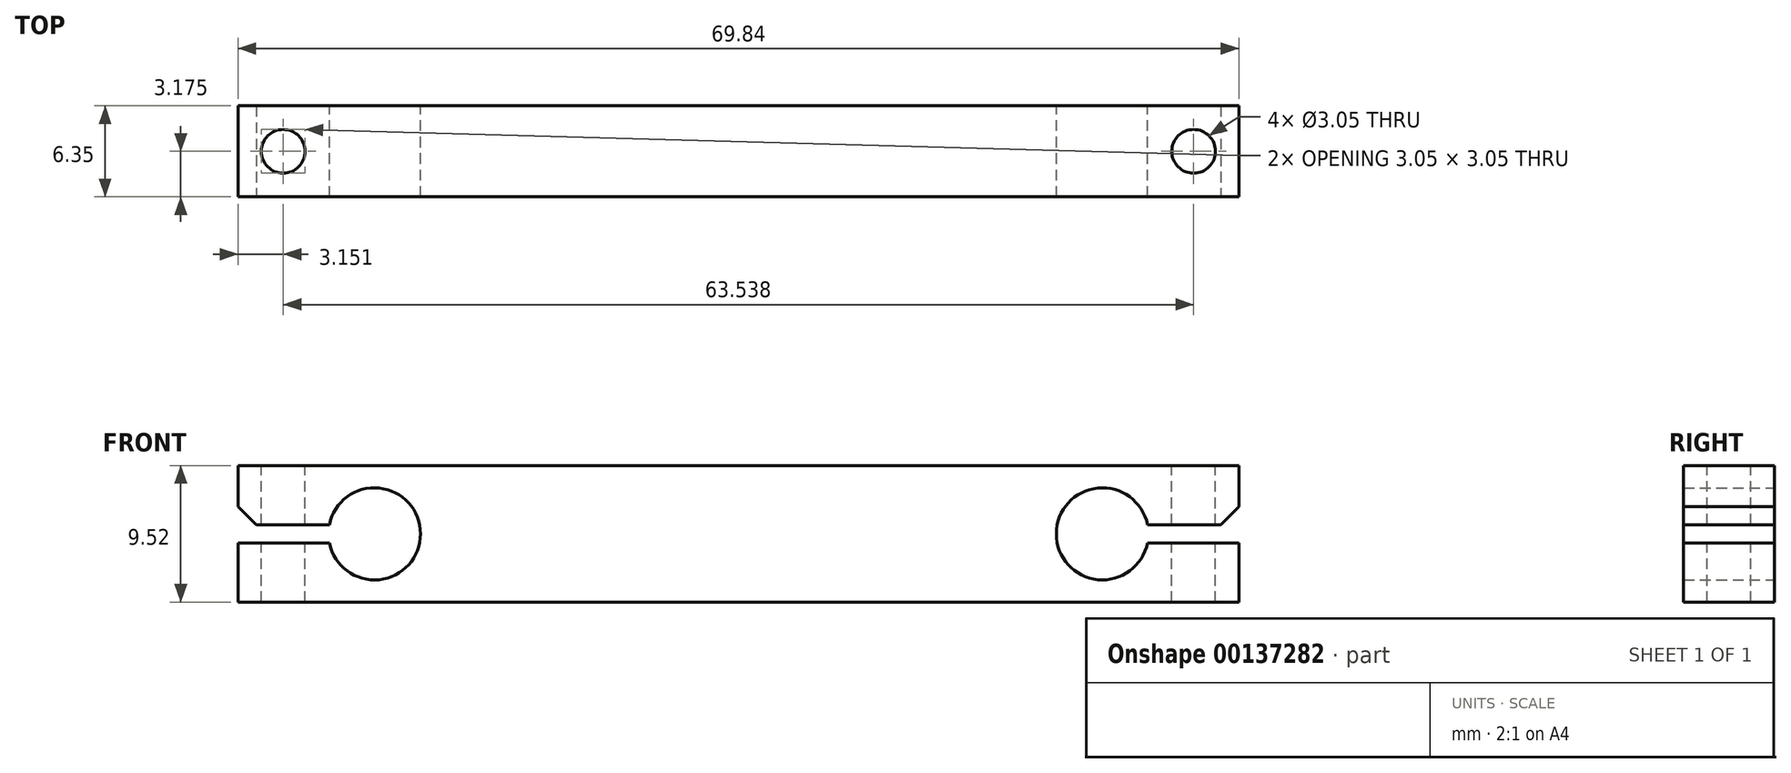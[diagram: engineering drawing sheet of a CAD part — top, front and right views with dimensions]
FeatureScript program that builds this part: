
annotation { "Feature Type Name" : "Feature", "Feature Type Description" : "" }
export const myFeature = defineFeature(function(context is Context, id is Id, definition is map)
    precondition{}
    {
        {
            var Q0;
            Q0=qCreatedBy(makeId("Front.planeOp"),FACE);
            var sketch = newSketch(context, id + "F0", { "sketchPlane" : qUnion([Q0])});
            skCircle(sketch, "E0", {"center": v(25.4, 0) * mm, "radius": 3.21 * mm});
            skLineSegment(sketch, "E1.bottom", {"start": v(0, 4.76) * mm, "end": v(34.93, 4.76) * mm});
            skLineSegment(sketch, "E1.top", {"start": v(0, -4.76) * mm, "end": v(34.93, -4.76) * mm});
            skLineSegment(sketch, "E1.left", {"start": v(0, 4.76) * mm, "end": v(0, -4.76) * mm});
            skLineSegment(sketch, "E1.right", {"start": v(34.93, 4.76) * mm, "end": v(34.93, -4.76) * mm});
            skPoint(sketch, "E1.middle", {"position": v(17.46, 0) * mm});
            skSolve(sketch);
        }
        {
            var Q0;
            Q0 = qSketchRegion(id + "F0", true);
            extrude(context, id + "F1", {"entities" : qUnion([Q0]), "depth" : 6.35 * mm});
        }
        {
            var Q0;
            Q0=makeQuery(id+"F1.opExtrude","SWEPT_FACE",FACE,{"disambiguationData":[OSD([sQuery(id+"F0.wireOp",EDGE,"E1.bottom")])]});
            var sketch = newSketch(context, id + "F2", { "sketchPlane" : qUnion([Q0])});
            skLineSegment(sketch, "E2.0", {"start": v(28.61, 0) * mm, "end": v(22.19, 0) * mm});
            skLineSegment(sketch, "E3", {"start": v(28.61, 0) * mm, "end": v(28.61, -6.35) * mm, "construction": true});
            skLineSegment(sketch, "E4", {"start": v(28.61, -3.18) * mm, "end": v(34.93, -3.18) * mm, "construction": true});
            skCircle(sketch, "E5", {"center": v(31.77, -3.18) * mm, "radius": 1.52 * mm});
            skSolve(sketch);
        }
        {
            var Q0;
            Q0=makeQuery(id+"F2.imprint","IMPRINT",FACE,{"disambiguationData":[TD([[makeQuery(id+"F2.imprint","IMPRINT",EDGE,{"derivedFrom":sQuery(id+"F2.wireOp",EDGE,"E5")}),1.0]])]});
            extrude(context, id + "F3", {"entities" : qUnion([Q0]), "operationType" : NewBodyOperationType.REMOVE, "endBound" : BoundingType.UP_TO_NEXT, "oppositeDirection" : true, "depth" : 25.4 * mm});
        }
        {
            var Q0;
            Q0=makeQuery(id+"F1.opExtrude","CAP_FACE",FACE,{"disambiguationData":[OSD([sQuery(id+"F0.wireOp",EDGE,"E0"),sQuery(id+"F0.wireOp",EDGE,"E1.bottom"),sQuery(id+"F0.wireOp",EDGE,"E1.top"),sQuery(id+"F0.wireOp",EDGE,"E1.left"),sQuery(id+"F0.wireOp",EDGE,"E1.right")])],"isStart":true});
            var sketch = newSketch(context, id + "F4", { "sketchPlane" : qUnion([Q0])});
            skLineSegment(sketch, "E6.bottom", {"start": v(-34.93, 0.63) * mm, "end": v(-28.55, 0.63) * mm});
            skLineSegment(sketch, "E6.top", {"start": v(-34.93, -0.64) * mm, "end": v(-28.55, -0.64) * mm});
            skLineSegment(sketch, "E6.left", {"start": v(-34.93, 0.63) * mm, "end": v(-34.93, -0.64) * mm});
            skLineSegment(sketch, "E6.right", {"start": v(-28.55, 0.63) * mm, "end": v(-28.55, -0.64) * mm});
            skPoint(sketch, "E6.middle", {"position": v(-31.74, 0) * mm});
            skSolve(sketch);
        }
        {
            var Q0;
            {var subQ0=sQuery(id+"F4.wireOp",EDGE,"E6.bottom");Q0=makeQuery(id+"F4.imprint","IMPRINT",FACE,{"disambiguationData":[TD([[makeQuery(id+"F4.imprint","IMPRINT",EDGE,{"derivedFrom":subQ0}),-1.0]])]});}
            extrude(context, id + "F5", {"entities" : qUnion([Q0]), "operationType" : NewBodyOperationType.REMOVE, "endBound" : BoundingType.THROUGH_ALL, "oppositeDirection" : true, "depth" : 25.4 * mm});
        }
        {
            var Q0;
            Q0=makeQuery(id+"F5.boolean.opBoolean","COPY",EDGE,{"derivedFrom":makeQuery(id+"F5.opExtrude","SWEPT_EDGE",EDGE,{"disambiguationData":[OSD([sQuery(id+"F0.wireOp",EDGE,"E1.right"),sQuery(id+"F4.wireOp",EDGE,"E6.bottom"),sQuery(id+"F4.wireOp",EDGE,"E6.left")])]})});
            var Q1;
            Q1=makeQuery(id+"F5.boolean.opBoolean","COPY",EDGE,{"derivedFrom":makeQuery(id+"F5.opExtrude","SWEPT_EDGE",EDGE,{"disambiguationData":[OSD([sQuery(id+"F0.wireOp",EDGE,"E1.right"),sQuery(id+"F4.wireOp",EDGE,"E6.top"),sQuery(id+"F4.wireOp",EDGE,"E6.left")])]})});
            chamfer(context, id + "F6", {"entities" : qUnion([Q0, Q1]), "width" : 1.27 * mm, "tangentPropagation" : true});
        }
        {
            var Q0;
            Q0=makeQuery(id+"F1.opExtrude","SWEPT_BODY",BODY,{"disambiguationData":[OSD([sQuery(id+"F0.wireOp",EDGE,"E0"),sQuery(id+"F0.wireOp",EDGE,"E1.bottom"),sQuery(id+"F0.wireOp",EDGE,"E1.top"),sQuery(id+"F0.wireOp",EDGE,"E1.left"),sQuery(id+"F0.wireOp",EDGE,"E1.right")])]});
            var Q1;
            Q1=makeQuery(id+"F1.opExtrude","SWEPT_FACE",FACE,{"disambiguationData":[OSD([sQuery(id+"F0.wireOp",EDGE,"E1.left")])]});
            mirror(context, id + "F7", {"operationType" : NewBodyOperationType.ADD, "entities" : qUnion([Q0]), "mirrorPlane" : qUnion([Q1])});
        }
    });
